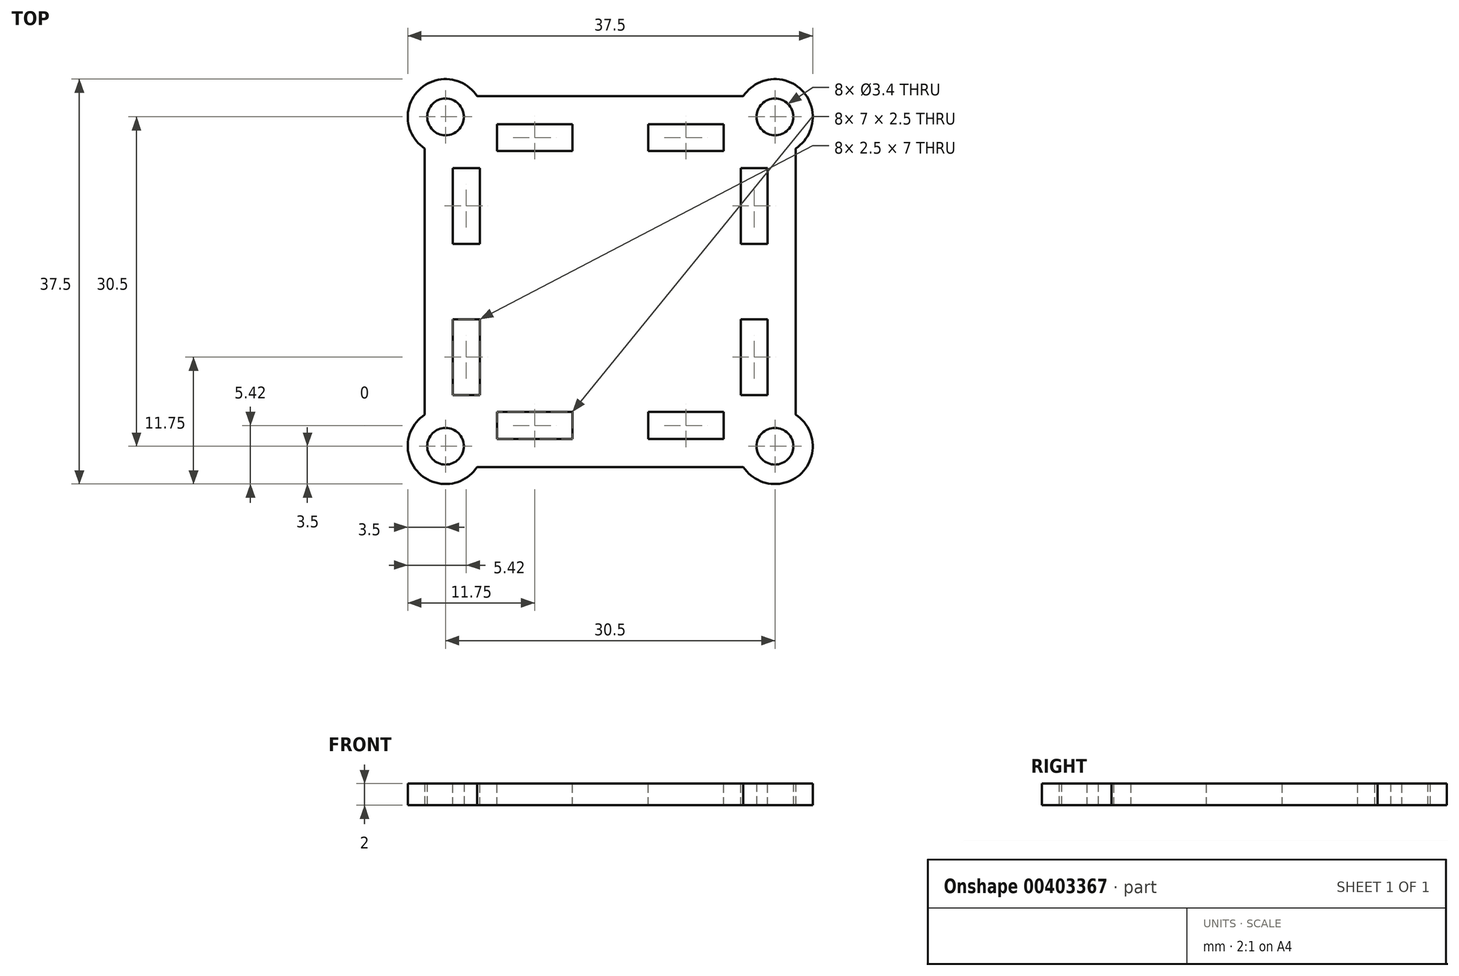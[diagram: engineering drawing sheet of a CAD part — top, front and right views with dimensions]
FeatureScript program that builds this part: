
annotation { "Feature Type Name" : "Feature", "Feature Type Description" : "" }
export const myFeature = defineFeature(function(context is Context, id is Id, definition is map)
    precondition{}
    {
        {
            assignVariable(context, id + "F0", {"name" : "padThickness", "anyValue" : 2});
        }
        {
            var Q0;
            Q0=qCreatedBy(makeId("Top.planeOp"),FACE);
            var sketch = newSketch(context, id + "F1", { "sketchPlane" : qUnion([Q0])});
            skLineSegment(sketch, "E0.bottom", {"start": v(15.25, -15.25) * mm, "end": v(-15.25, -15.25) * mm});
            skLineSegment(sketch, "E0.top", {"start": v(15.25, 15.25) * mm, "end": v(-15.25, 15.25) * mm});
            skLineSegment(sketch, "E0.left", {"start": v(15.25, -15.25) * mm, "end": v(15.25, 15.25) * mm});
            skLineSegment(sketch, "E0.right", {"start": v(-15.25, -15.25) * mm, "end": v(-15.25, 15.25) * mm});
            skPoint(sketch, "E0.middle", {"position": v(0, 0) * mm});
            skCircle(sketch, "E1", {"center": v(-15.25, 15.25) * mm, "radius": 1.7 * mm});
            skLineSegment(sketch, "E2", {"start": v(0, 15.25) * mm, "end": v(0, -15.25) * mm, "construction": true});
            skLineSegment(sketch, "E3", {"start": v(-15.25, 0) * mm, "end": v(15.25, 0) * mm, "construction": true});
            skCircle(sketch, "E4.MirrorC", {"center": v(15.25, 15.25) * mm, "radius": 1.7 * mm});
            skLineSegment(sketch, "E5.MirrorCS", {"start": v(15.25, 0) * mm, "end": v(-15.25, 0) * mm, "construction": true});
            skCircle(sketch, "E6.MirrorC", {"center": v(15.25, -15.25) * mm, "radius": 1.7 * mm});
            skCircle(sketch, "E7.MirrorC", {"center": v(-15.25, -15.25) * mm, "radius": 1.7 * mm});
            skCircle(sketch, "E8", {"center": v(-15.25, 15.25) * mm, "radius": 3.5 * mm});
            skCircle(sketch, "E9.MirrorC", {"center": v(15.25, 15.25) * mm, "radius": 3.5 * mm});
            skCircle(sketch, "E10.MirrorC", {"center": v(15.25, -15.25) * mm, "radius": 3.5 * mm});
            skCircle(sketch, "E11.MirrorC", {"center": v(-15.25, -15.25) * mm, "radius": 3.5 * mm});
            skLineSegment(sketch, "E12", {"start": v(-10.5, 15.25) * mm, "end": v(-10.5, -15.25) * mm, "construction": true});
            skLineSegment(sketch, "E13", {"start": v(10.5, 15.25) * mm, "end": v(10.5, -15.25) * mm, "construction": true});
            skLineSegment(sketch, "E14", {"start": v(-15.25, 17) * mm, "end": v(15.25, 17) * mm, "construction": true});
            skLineSegment(sketch, "E15", {"start": v(-15.25, -17) * mm, "end": v(15.25, -17) * mm, "construction": true});
            skLineSegment(sketch, "E16", {"start": v(-17.17, 12.32) * mm, "end": v(-17.17, -12.32) * mm});
            skLineSegment(sketch, "E17", {"start": v(-13.33, -12.32) * mm, "end": v(-13.33, 12.32) * mm});
            skLineSegment(sketch, "E18", {"start": v(-12.32, 17.17) * mm, "end": v(12.32, 17.17) * mm});
            skLineSegment(sketch, "E19", {"start": v(-12.32, 13.33) * mm, "end": v(12.32, 13.33) * mm});
            skLineSegment(sketch, "E20.MirrorCS", {"start": v(-12.32, -17.17) * mm, "end": v(12.32, -17.17) * mm});
            skLineSegment(sketch, "E21.MirrorCS", {"start": v(-12.32, -13.33) * mm, "end": v(12.32, -13.33) * mm});
            skLineSegment(sketch, "E22.MirrorCS", {"start": v(17.17, 12.32) * mm, "end": v(17.17, -12.32) * mm});
            skLineSegment(sketch, "E23.MirrorCS", {"start": v(13.33, -12.32) * mm, "end": v(13.33, 12.32) * mm});
            skPoint(sketch, "E24", {"position": v(0, 17) * mm});
            skPoint(sketch, "E25", {"position": v(0, 18.92) * mm});
            skSolve(sketch);
        }
        {
            var Q0;
            {var subQ1=sQuery(id+"F1.wireOp",EDGE,"E0.top");var subQ5=sQuery(id+"F1.wireOp",EDGE,"E8");var subQ7=makeQuery(id+"F1.imprint","INTERSECT",VERTEX,{"derivedFrom":[subQ1,subQ5]});Q0=makeQuery(id+"F1.imprint","IMPRINT",FACE,{"disambiguationData":[TD([[makeQuery(id+"F1.imprint","IMPRINT",EDGE,{"disambiguationData":[TD([[subQ7,-1.0]])],"derivedFrom":subQ1}),-1.0]])]});}
            var Q1;
            {var subQ0=sQuery(id+"F1.wireOp",EDGE,"E8");var subQ5=sQuery(id+"F1.wireOp",EDGE,"E0.top");var subQ9=makeQuery(id+"F1.imprint","INTERSECT",VERTEX,{"derivedFrom":[subQ5,subQ0]});Q1=makeQuery(id+"F1.imprint","IMPRINT",FACE,{"disambiguationData":[TD([[makeQuery(id+"F1.imprint","IMPRINT",EDGE,{"disambiguationData":[TD([[subQ9,-1.0]])],"derivedFrom":subQ5}),1.0]])]});}
            var Q2;
            {var subQ2=sQuery(id+"F1.wireOp",EDGE,"E0.top");var subQ4=sQuery(id+"F1.wireOp",EDGE,"E4.MirrorC");var subQ5=makeQuery(id+"F1.imprint","INTERSECT",VERTEX,{"derivedFrom":[subQ2,subQ4]});Q2=makeQuery(id+"F1.imprint","IMPRINT",FACE,{"disambiguationData":[TD([[makeQuery(id+"F1.imprint","IMPRINT",EDGE,{"disambiguationData":[TD([[subQ5,-1.0]])],"derivedFrom":subQ2}),-1.0]])]});}
            var Q3;
            {var subQ4=sQuery(id+"F1.wireOp",EDGE,"E4.MirrorC");var subQ5=sQuery(id+"F1.wireOp",EDGE,"E0.top");var subQ6=makeQuery(id+"F1.imprint","INTERSECT",VERTEX,{"derivedFrom":[subQ5,subQ4]});Q3=makeQuery(id+"F1.imprint","IMPRINT",FACE,{"disambiguationData":[TD([[makeQuery(id+"F1.imprint","IMPRINT",EDGE,{"disambiguationData":[TD([[subQ6,-1.0]])],"derivedFrom":subQ5}),1.0]])]});}
            var Q4;
            {var subQ5=sQuery(id+"F1.wireOp",EDGE,"E23.MirrorCS");Q4=makeQuery(id+"F1.imprint","IMPRINT",FACE,{"disambiguationData":[TD([[makeQuery(id+"F1.imprint","IMPRINT",EDGE,{"derivedFrom":subQ5}),-1.0]])]});}
            var Q5;
            {var subQ5=sQuery(id+"F1.wireOp",EDGE,"E19");Q5=makeQuery(id+"F1.imprint","IMPRINT",FACE,{"disambiguationData":[TD([[makeQuery(id+"F1.imprint","IMPRINT",EDGE,{"derivedFrom":subQ5}),1.0]])]});}
            var Q6;
            {var subQ5=sQuery(id+"F1.wireOp",EDGE,"E17");Q6=makeQuery(id+"F1.imprint","IMPRINT",FACE,{"disambiguationData":[TD([[makeQuery(id+"F1.imprint","IMPRINT",EDGE,{"derivedFrom":subQ5}),1.0]])]});}
            var Q7;
            {var subQ5=sQuery(id+"F1.wireOp",EDGE,"E16");Q7=makeQuery(id+"F1.imprint","IMPRINT",FACE,{"disambiguationData":[TD([[makeQuery(id+"F1.imprint","IMPRINT",EDGE,{"derivedFrom":subQ5}),1.0]])]});}
            var Q8;
            {var subQ5=sQuery(id+"F1.wireOp",EDGE,"E22.MirrorCS");Q8=makeQuery(id+"F1.imprint","IMPRINT",FACE,{"disambiguationData":[TD([[makeQuery(id+"F1.imprint","IMPRINT",EDGE,{"derivedFrom":subQ5}),-1.0]])]});}
            var Q9;
            {var subQ5=sQuery(id+"F1.wireOp",EDGE,"E21.MirrorCS");Q9=makeQuery(id+"F1.imprint","IMPRINT",FACE,{"disambiguationData":[TD([[makeQuery(id+"F1.imprint","IMPRINT",EDGE,{"derivedFrom":subQ5}),-1.0]])]});}
            var Q10;
            {var subQ5=sQuery(id+"F1.wireOp",EDGE,"E20.MirrorCS");Q10=makeQuery(id+"F1.imprint","IMPRINT",FACE,{"disambiguationData":[TD([[makeQuery(id+"F1.imprint","IMPRINT",EDGE,{"derivedFrom":subQ5}),1.0]])]});}
            var Q11;
            {var subQ5=sQuery(id+"F1.wireOp",EDGE,"E18");Q11=makeQuery(id+"F1.imprint","IMPRINT",FACE,{"disambiguationData":[TD([[makeQuery(id+"F1.imprint","IMPRINT",EDGE,{"derivedFrom":subQ5}),-1.0]])]});}
            var Q12;
            {var subQ0=sQuery(id+"F1.wireOp",EDGE,"E11.MirrorC");var subQ2=sQuery(id+"F1.wireOp",EDGE,"E0.bottom");var subQ3=makeQuery(id+"F1.imprint","INTERSECT",VERTEX,{"derivedFrom":[subQ2,subQ0]});Q12=makeQuery(id+"F1.imprint","IMPRINT",FACE,{"disambiguationData":[TD([[makeQuery(id+"F1.imprint","IMPRINT",EDGE,{"disambiguationData":[TD([[subQ3,-1.0]])],"derivedFrom":subQ2}),1.0]])]});}
            var Q13;
            {var subQ0=sQuery(id+"F1.wireOp",EDGE,"E11.MirrorC");var subQ5=sQuery(id+"F1.wireOp",EDGE,"E0.bottom");var subQ8=makeQuery(id+"F1.imprint","INTERSECT",VERTEX,{"derivedFrom":[subQ5,subQ0]});Q13=makeQuery(id+"F1.imprint","IMPRINT",FACE,{"disambiguationData":[TD([[makeQuery(id+"F1.imprint","IMPRINT",EDGE,{"disambiguationData":[TD([[subQ8,-1.0]])],"derivedFrom":subQ5}),-1.0]])]});}
            var Q14;
            {var subQ4=sQuery(id+"F1.wireOp",EDGE,"E6.MirrorC");var subQ5=sQuery(id+"F1.wireOp",EDGE,"E0.bottom");var subQ6=makeQuery(id+"F1.imprint","INTERSECT",VERTEX,{"derivedFrom":[subQ5,subQ4]});Q14=makeQuery(id+"F1.imprint","IMPRINT",FACE,{"disambiguationData":[TD([[makeQuery(id+"F1.imprint","IMPRINT",EDGE,{"disambiguationData":[TD([[subQ6,-1.0]])],"derivedFrom":subQ5}),-1.0]])]});}
            var Q15;
            {var subQ2=sQuery(id+"F1.wireOp",EDGE,"E0.bottom");var subQ4=sQuery(id+"F1.wireOp",EDGE,"E6.MirrorC");var subQ5=makeQuery(id+"F1.imprint","INTERSECT",VERTEX,{"derivedFrom":[subQ2,subQ4]});Q15=makeQuery(id+"F1.imprint","IMPRINT",FACE,{"disambiguationData":[TD([[makeQuery(id+"F1.imprint","IMPRINT",EDGE,{"disambiguationData":[TD([[subQ5,-1.0]])],"derivedFrom":subQ2}),1.0]])]});}
            var Q16;
            {var subQ0=sQuery(id+"F1.wireOp",EDGE,"E17");Q16=makeQuery(id+"F1.imprint","IMPRINT",FACE,{"disambiguationData":[TD([[makeQuery(id+"F1.imprint","IMPRINT",EDGE,{"derivedFrom":subQ0}),-1.0]])]});}
            extrude(context, id + "F2", {"entities" : qUnion([Q0, Q1, Q2, Q3, Q4, Q5, Q6, Q7, Q8, Q9, Q10, Q11, Q12, Q13, Q14, Q15, Q16]), "depth" : (getVariable(context, 'padThickness')) * mm});
        }
        {
            var Q0;
            Q0=qCreatedBy(makeId("Front.planeOp"),FACE);
            var sketch = newSketch(context, id + "F3", { "sketchPlane" : qUnion([Q0])});
            skLineSegment(sketch, "E26", {"start": v(0, 0) * mm, "end": v(0, 87.17) * mm, "construction": true});
            skSolve(sketch);
        }
        {
            var Q0;
            Q0=makeQuery(id+"F2.opExtrude","SWEPT_BODY",BODY,{"disambiguationData":[OSD([sQuery(id+"F1.wireOp",EDGE,"E1"),sQuery(id+"F1.wireOp",EDGE,"E4.MirrorC"),sQuery(id+"F1.wireOp",EDGE,"E6.MirrorC"),sQuery(id+"F1.wireOp",EDGE,"E7.MirrorC"),sQuery(id+"F1.wireOp",EDGE,"E8"),sQuery(id+"F1.wireOp",EDGE,"E9.MirrorC"),sQuery(id+"F1.wireOp",EDGE,"E10.MirrorC"),sQuery(id+"F1.wireOp",EDGE,"E11.MirrorC"),sQuery(id+"F1.wireOp",EDGE,"E16"),sQuery(id+"F1.wireOp",EDGE,"E18"),sQuery(id+"F1.wireOp",EDGE,"E20.MirrorCS"),sQuery(id+"F1.wireOp",EDGE,"E22.MirrorCS")])]});
            var Q1;
            Q1=sQuery(id+"F3.wireOp",EDGE,"E26");
            transform(context, id + "F4", {"entities" : qUnion([Q0]), "transformType" : TransformType.ROTATION, "transformAxis" : qUnion([Q1]), "angle" : 45 * degree, "makeCopy" : true});
        }
        {
            var Q0;
            Q0=makeQuery(id+"F2.opExtrude","SWEPT_BODY",BODY,{"disambiguationData":[OSD([sQuery(id+"F1.wireOp",EDGE,"E1"),sQuery(id+"F1.wireOp",EDGE,"E4.MirrorC"),sQuery(id+"F1.wireOp",EDGE,"E6.MirrorC"),sQuery(id+"F1.wireOp",EDGE,"E7.MirrorC"),sQuery(id+"F1.wireOp",EDGE,"E8"),sQuery(id+"F1.wireOp",EDGE,"E9.MirrorC"),sQuery(id+"F1.wireOp",EDGE,"E10.MirrorC"),sQuery(id+"F1.wireOp",EDGE,"E11.MirrorC"),sQuery(id+"F1.wireOp",EDGE,"E16"),sQuery(id+"F1.wireOp",EDGE,"E18"),sQuery(id+"F1.wireOp",EDGE,"E20.MirrorCS"),sQuery(id+"F1.wireOp",EDGE,"E22.MirrorCS")])]});
            var Q1;
            Q1=makeQuery(id+"F4.opPattern","COPY",BODY,{"derivedFrom":makeQuery(id+"F2.opExtrude","SWEPT_BODY",BODY,{"disambiguationData":[OSD([sQuery(id+"F1.wireOp",EDGE,"E1"),sQuery(id+"F1.wireOp",EDGE,"E4.MirrorC"),sQuery(id+"F1.wireOp",EDGE,"E6.MirrorC"),sQuery(id+"F1.wireOp",EDGE,"E7.MirrorC"),sQuery(id+"F1.wireOp",EDGE,"E8"),sQuery(id+"F1.wireOp",EDGE,"E9.MirrorC"),sQuery(id+"F1.wireOp",EDGE,"E10.MirrorC"),sQuery(id+"F1.wireOp",EDGE,"E11.MirrorC"),sQuery(id+"F1.wireOp",EDGE,"E16"),sQuery(id+"F1.wireOp",EDGE,"E18"),sQuery(id+"F1.wireOp",EDGE,"E20.MirrorCS"),sQuery(id+"F1.wireOp",EDGE,"E22.MirrorCS")])]}),"instanceName":"1"});
            booleanBodies(context, id + "F5", {"operationType" : BooleanOperationType.UNION, "tools" : qUnion([Q0, Q1])});
        }
        {
            var Q0;
            Q0=makeQuery(id+"F2.opExtrude","CAP_FACE",FACE,{"disambiguationData":[OSD([sQuery(id+"F1.wireOp",EDGE,"E1"),sQuery(id+"F1.wireOp",EDGE,"E4.MirrorC"),sQuery(id+"F1.wireOp",EDGE,"E6.MirrorC"),sQuery(id+"F1.wireOp",EDGE,"E7.MirrorC"),sQuery(id+"F1.wireOp",EDGE,"E8"),sQuery(id+"F1.wireOp",EDGE,"E9.MirrorC"),sQuery(id+"F1.wireOp",EDGE,"E10.MirrorC"),sQuery(id+"F1.wireOp",EDGE,"E11.MirrorC"),sQuery(id+"F1.wireOp",EDGE,"E16"),sQuery(id+"F1.wireOp",EDGE,"E18"),sQuery(id+"F1.wireOp",EDGE,"E20.MirrorCS"),sQuery(id+"F1.wireOp",EDGE,"E22.MirrorCS")])],"isStart":false});
            var sketch = newSketch(context, id + "F6", { "sketchPlane" : qUnion([Q0])});
            skLineSegment(sketch, "E27.0", {"start": v(-10.5, 15.25) * mm, "end": v(-10.5, -15.25) * mm, "construction": true});
            skLineSegment(sketch, "E27.1", {"start": v(-12.32, 13.33) * mm, "end": v(12.32, 13.33) * mm, "construction": true});
            skLineSegment(sketch, "E27.2", {"start": v(10.5, 15.25) * mm, "end": v(10.5, -15.25) * mm, "construction": true});
            skLineSegment(sketch, "E27.3", {"start": v(-12.32, -13.33) * mm, "end": v(12.32, -13.33) * mm, "construction": true});
            skText(sketch, "E28", { "text": "tits", "fontName": "AllertaStencil-Regular.ttf"});
            skPoint(sketch, "E29", {"position": v(0, 0) * mm});
            const initialGuessF6  = {"E28": [-0.015, -0.00666, 1, 0, 0.01332]};
            skSetInitialGuess(sketch, initialGuessF6);
            skSolve(sketch);
        }
        {
            var Q0;
            {var subQ0=makeQuery(id+"F2.opExtrude","CAP_FACE",FACE,{"disambiguationData":[OSD([sQuery(id+"F1.wireOp",EDGE,"E1"),sQuery(id+"F1.wireOp",EDGE,"E4.MirrorC"),sQuery(id+"F1.wireOp",EDGE,"E6.MirrorC"),sQuery(id+"F1.wireOp",EDGE,"E7.MirrorC"),sQuery(id+"F1.wireOp",EDGE,"E8"),sQuery(id+"F1.wireOp",EDGE,"E9.MirrorC"),sQuery(id+"F1.wireOp",EDGE,"E10.MirrorC"),sQuery(id+"F1.wireOp",EDGE,"E11.MirrorC"),sQuery(id+"F1.wireOp",EDGE,"E16"),sQuery(id+"F1.wireOp",EDGE,"E18"),sQuery(id+"F1.wireOp",EDGE,"E20.MirrorCS"),sQuery(id+"F1.wireOp",EDGE,"E22.MirrorCS")])],"isStart":false});Q0=makeQuery(id+"F5.opBoolean","MERGE",FACE,{"derivedFrom":[subQ0,makeQuery(id+"F4.opPattern","COPY",FACE,{"derivedFrom":subQ0,"instanceName":"1"})]});}
            var sketch = newSketch(context, id + "F7", { "sketchPlane" : qUnion([Q0])});
            skLineSegment(sketch, "E30.0", {"start": v(15.25, -15.25) * mm, "end": v(15.25, 15.25) * mm, "construction": true});
            skLineSegment(sketch, "E30.1", {"start": v(15.25, 15.25) * mm, "end": v(-15.25, 15.25) * mm, "construction": true});
            skLineSegment(sketch, "E30.2", {"start": v(-15.25, -15.25) * mm, "end": v(-15.25, 15.25) * mm, "construction": true});
            skLineSegment(sketch, "E30.3", {"start": v(15.25, -15.25) * mm, "end": v(-15.25, -15.25) * mm, "construction": true});
            skLineSegment(sketch, "E31", {"start": v(-15.25, 15.25) * mm, "end": v(15.25, -15.25) * mm, "construction": true});
            skLineSegment(sketch, "E32", {"start": v(21.57, 0) * mm, "end": v(-21.57, 0) * mm, "construction": true});
            skLineSegment(sketch, "E33", {"start": v(0, 21.57) * mm, "end": v(0, -21.57) * mm, "construction": true});
            skLineSegment(sketch, "E34", {"start": v(-15.25, -15.25) * mm, "end": v(15.25, 15.25) * mm, "construction": true});
            skCircle(sketch, "E35.0", {"center": v(-15.25, 15.25) * mm, "radius": 3.5 * mm, "construction": true});
            skLineSegment(sketch, "E36.0", {"start": v(-13.33, -12.32) * mm, "end": v(-13.33, -5.63) * mm, "construction": true});
            skLineSegment(sketch, "E37.0", {"start": v(-10.61, 13.33) * mm, "end": v(10.61, 13.33) * mm});
            skLineSegment(sketch, "E37.1", {"start": v(13.33, -12.32) * mm, "end": v(13.33, -5.63) * mm, "construction": true});
            skLineSegment(sketch, "E38.0", {"start": v(-10.61, -13.33) * mm, "end": v(10.61, -13.33) * mm});
            skCircle(sketch, "E39.0", {"center": v(15.25, -15.25) * mm, "radius": 3.5 * mm, "construction": true});
            skCircle(sketch, "E40.0", {"center": v(-15.25, -15.25) * mm, "radius": 3.5 * mm, "construction": true});
            skLineSegment(sketch, "E41.0", {"start": v(-12.32, 17.17) * mm, "end": v(12.32, 17.17) * mm});
            skLineSegment(sketch, "E42.0", {"start": v(-15.25, -17) * mm, "end": v(15.25, -17) * mm, "construction": true});
            skLineSegment(sketch, "E43.0", {"start": v(-17.17, 12.32) * mm, "end": v(-17.17, -12.32) * mm, "construction": true});
            skLineSegment(sketch, "E44.0", {"start": v(17.17, 12.32) * mm, "end": v(17.17, -12.32) * mm, "construction": true});
            skPoint(sketch, "E45", {"position": v(-12.32, 13.33) * mm});
            skPoint(sketch, "E46", {"position": v(-13.33, 12.32) * mm});
            skCircle(sketch, "E47.0", {"center": v(15.25, 15.25) * mm, "radius": 3.5 * mm, "construction": true});
            skLineSegment(sketch, "E48", {"start": v(-17.17, 7.11) * mm, "end": v(-1.92, 7.11) * mm, "construction": true});
            skLineSegment(sketch, "E49", {"start": v(-17.17, -7.11) * mm, "end": v(-1.92, -7.11) * mm, "construction": true});
            skPoint(sketch, "E50", {"position": v(0, 7.11) * mm});
            skPoint(sketch, "E51", {"position": v(0, -7.11) * mm});
            skArc(sketch, "E52", {"start": v(13.33, 5.63) * mm, "mid": v(11.24, 6.06) * mm, "end": v(9.14, 6.42) * mm});
            skPoint(sketch, "E53", {"position": v(-13.33, 5.63) * mm});
            skPoint(sketch, "E54", {"position": v(13.33, 5.63) * mm});
            skPoint(sketch, "E55.MirrorP", {"position": v(13.33, -5.63) * mm});
            skPoint(sketch, "E56.MirrorP", {"position": v(-13.33, -5.63) * mm});
            skArc(sketch, "E57.MirrorCS", {"start": v(13.33, -5.63) * mm, "mid": v(11.24, -6.06) * mm, "end": v(9.14, -6.42) * mm});
            skPoint(sketch, "E58.trimOffspring.end.orphan", {"position": v(-20.86, 3.43) * mm});
            skPoint(sketch, "E59.orphan", {"position": v(20.86, 3.43) * mm});
            skPoint(sketch, "E60.orphan", {"position": v(20.86, -3.43) * mm});
            skPoint(sketch, "E61.orphan", {"position": v(-20.86, -3.43) * mm});
            skLineSegment(sketch, "E62.0", {"start": v(-1.92, 13.33) * mm, "end": v(-1.92, 7.08) * mm});
            skPoint(sketch, "E63.orphan", {"position": v(-1.92, 21.57) * mm});
            skPoint(sketch, "E64.orphan", {"position": v(1.92, 21.57) * mm});
            skPoint(sketch, "E65.orphan", {"position": v(1.92, -21.57) * mm});
            skPoint(sketch, "E66.orphan", {"position": v(-1.92, -21.57) * mm});
            skLineSegment(sketch, "E67.0", {"start": v(-10.61, 13.33) * mm, "end": v(16.6, -13.9) * mm, "construction": true});
            skLineSegment(sketch, "E68.MirrorCS", {"start": v(-13.33, 10.61) * mm, "end": v(13.9, -16.6) * mm, "construction": true});
            skPoint(sketch, "E69.orphan", {"position": v(-13.9, 16.6) * mm});
            skPoint(sketch, "E70.orphan", {"position": v(-16.6, 13.9) * mm});
            skLineSegment(sketch, "E71.0", {"start": v(-16.6, -13.9) * mm, "end": v(-15.25, -12.53) * mm, "construction": true});
            skLineSegment(sketch, "E72.MirrorCS", {"start": v(-13.9, -16.6) * mm, "end": v(16.6, 13.9) * mm, "construction": true});
            skPoint(sketch, "E73.orphan", {"position": v(12.32, 13.33) * mm});
            skPoint(sketch, "E74.orphan", {"position": v(13.33, 12.32) * mm});
            skPoint(sketch, "E75.orphan", {"position": v(-12.32, -13.33) * mm});
            skPoint(sketch, "E76.orphan", {"position": v(12.32, -13.33) * mm});
            skLineSegment(sketch, "E77.trimOffspring", {"start": v(-13.33, 5.63) * mm, "end": v(-13.33, 10.61) * mm, "construction": true});
            skLineSegment(sketch, "E78.trimOffspring", {"start": v(13.33, 5.63) * mm, "end": v(13.33, 10.61) * mm, "construction": true});
            skLineSegment(sketch, "E79", {"start": v(-13.33, 10.61) * mm, "end": v(-13.33, 5.63) * mm});
            skLineSegment(sketch, "E80", {"start": v(-13.33, -5.63) * mm, "end": v(-13.33, -10.61) * mm});
            skLineSegment(sketch, "E81.trimOffspring", {"start": v(-14.54, -11.82) * mm, "end": v(13.9, 16.6) * mm, "construction": true});
            skLineSegment(sketch, "E82", {"start": v(-10.61, 13.33) * mm, "end": v(-4.25, 6.96) * mm});
            skLineSegment(sketch, "E83", {"start": v(-9.14, 6.42) * mm, "end": v(-13.33, 10.61) * mm});
            skLineSegment(sketch, "E84", {"start": v(10.61, 13.33) * mm, "end": v(4.25, 6.96) * mm});
            skLineSegment(sketch, "E85", {"start": v(13.33, 10.61) * mm, "end": v(9.14, 6.42) * mm});
            skLineSegment(sketch, "E86", {"start": v(-9.14, -6.42) * mm, "end": v(-13.33, -10.61) * mm});
            skLineSegment(sketch, "E87", {"start": v(-10.61, -13.33) * mm, "end": v(-4.25, -6.96) * mm});
            skLineSegment(sketch, "E88", {"start": v(4.25, -6.96) * mm, "end": v(10.61, -13.33) * mm});
            skLineSegment(sketch, "E89", {"start": v(9.14, -6.42) * mm, "end": v(13.33, -10.61) * mm});
            skLineSegment(sketch, "E90", {"start": v(13.33, -10.61) * mm, "end": v(13.33, -5.63) * mm});
            skLineSegment(sketch, "E91", {"start": v(13.33, 10.61) * mm, "end": v(13.33, 5.63) * mm});
            skLineSegment(sketch, "E92.MirrorCS", {"start": v(1.92, 13.33) * mm, "end": v(1.92, 7.08) * mm});
            skLineSegment(sketch, "E93.MirrorCS", {"start": v(-1.92, -13.33) * mm, "end": v(-1.92, -7.08) * mm});
            skLineSegment(sketch, "E94.MirrorCS", {"start": v(1.92, -13.33) * mm, "end": v(1.92, -7.08) * mm});
            skArc(sketch, "E95.trimOffspring", {"start": v(-9.14, 6.42) * mm, "mid": v(-11.24, 6.06) * mm, "end": v(-13.33, 5.63) * mm});
            skArc(sketch, "E96.trimOffspring", {"start": v(-1.92, 7.08) * mm, "mid": v(-3.08, 7.03) * mm, "end": v(-4.25, 6.96) * mm});
            skLineSegment(sketch, "E97.trimOffspring", {"start": v(0, 7.11) * mm, "end": v(17.17, 7.11) * mm, "construction": true});
            skArc(sketch, "E98.trimOffspring", {"start": v(4.25, 6.96) * mm, "mid": v(3.08, 7.03) * mm, "end": v(1.92, 7.08) * mm});
            skArc(sketch, "E99.trimOffspring", {"start": v(-9.14, -6.42) * mm, "mid": v(-11.24, -6.06) * mm, "end": v(-13.33, -5.63) * mm});
            skLineSegment(sketch, "E100.trimOffspring", {"start": v(1.92, -7.11) * mm, "end": v(17.17, -7.11) * mm, "construction": true});
            skArc(sketch, "E101.trimOffspring", {"start": v(4.25, -6.96) * mm, "mid": v(3.08, -7.03) * mm, "end": v(1.92, -7.08) * mm});
            skArc(sketch, "E102.trimOffspring", {"start": v(-1.92, -7.08) * mm, "mid": v(-3.08, -7.03) * mm, "end": v(-4.25, -6.96) * mm});
            skSolve(sketch);
        }
        {
            var Q0;
            {var subQ0=makeQuery(id+"F2.opExtrude","CAP_FACE",FACE,{"disambiguationData":[OSD([sQuery(id+"F1.wireOp",EDGE,"E1"),sQuery(id+"F1.wireOp",EDGE,"E4.MirrorC"),sQuery(id+"F1.wireOp",EDGE,"E6.MirrorC"),sQuery(id+"F1.wireOp",EDGE,"E7.MirrorC"),sQuery(id+"F1.wireOp",EDGE,"E8"),sQuery(id+"F1.wireOp",EDGE,"E9.MirrorC"),sQuery(id+"F1.wireOp",EDGE,"E10.MirrorC"),sQuery(id+"F1.wireOp",EDGE,"E11.MirrorC"),sQuery(id+"F1.wireOp",EDGE,"E16"),sQuery(id+"F1.wireOp",EDGE,"E18"),sQuery(id+"F1.wireOp",EDGE,"E20.MirrorCS"),sQuery(id+"F1.wireOp",EDGE,"E22.MirrorCS")])],"isStart":false});Q0=makeQuery(id+"F5.opBoolean","MERGE",FACE,{"derivedFrom":[subQ0,makeQuery(id+"F4.opPattern","COPY",FACE,{"derivedFrom":subQ0,"instanceName":"1"})]});}
            var sketch = newSketch(context, id + "F8", { "sketchPlane" : qUnion([Q0])});
            skLineSegment(sketch, "E103", {"start": v(-17.17, 7.11) * mm, "end": v(-17.17, -7.11) * mm});
            skLineSegment(sketch, "E104", {"start": v(-7.11, -17.17) * mm, "end": v(7.11, -17.17) * mm});
            skLineSegment(sketch, "E105", {"start": v(17.17, -7.11) * mm, "end": v(17.17, 7.11) * mm});
            skLineSegment(sketch, "E106", {"start": v(7.11, 17.17) * mm, "end": v(-7.11, 17.17) * mm});
            skSolve(sketch);
        }
        {
            var Q0;
            Q0=makeQuery(id+"F8.imprint","IMPRINT",FACE,{"disambiguationData":[TD([[makeQuery(id+"F8.imprint","IMPRINT",EDGE,{"derivedFrom":sQuery(id+"F8.wireOp",EDGE,"E106")}),-1.0]])]});
            var Q1;
            Q1=makeQuery(id+"F8.imprint","IMPRINT",FACE,{"disambiguationData":[TD([[makeQuery(id+"F8.imprint","IMPRINT",EDGE,{"derivedFrom":sQuery(id+"F8.wireOp",EDGE,"E105")}),-1.0]])]});
            var Q2;
            Q2=makeQuery(id+"F8.imprint","IMPRINT",FACE,{"disambiguationData":[TD([[makeQuery(id+"F8.imprint","IMPRINT",EDGE,{"derivedFrom":sQuery(id+"F8.wireOp",EDGE,"E104")}),-1.0]])]});
            var Q3;
            Q3=makeQuery(id+"F8.imprint","IMPRINT",FACE,{"disambiguationData":[TD([[makeQuery(id+"F8.imprint","IMPRINT",EDGE,{"derivedFrom":sQuery(id+"F8.wireOp",EDGE,"E103")}),-1.0]])]});
            extrude(context, id + "F9", {"entities" : qUnion([Q0, Q1, Q2, Q3]), "operationType" : NewBodyOperationType.REMOVE, "endBound" : BoundingType.THROUGH_ALL, "oppositeDirection" : true, "depth" : 25 * mm});
        }
        {
            var Q0;
            Q0=makeQuery(id+"F7.imprint","IMPRINT",FACE,{"disambiguationData":[TD([[makeQuery(id+"F7.imprint","IMPRINT",EDGE,{"derivedFrom":sQuery(id+"F7.wireOp",EDGE,"E52")}),1.0]])]});
            var sketch = newSketch(context, id + "F10", { "sketchPlane" : qUnion([Q0])});
            skLineSegment(sketch, "E107.0", {"start": v(0, 21.57) * mm, "end": v(0, -21.57) * mm, "construction": true});
            skLineSegment(sketch, "E108.0", {"start": v(21.57, 0) * mm, "end": v(-21.57, 0) * mm, "construction": true});
            skLineSegment(sketch, "E109.0", {"start": v(-12.32, 17.17) * mm, "end": v(12.32, 17.17) * mm});
            skLineSegment(sketch, "E110.0", {"start": v(-17.17, 12.32) * mm, "end": v(-17.17, -12.32) * mm, "construction": true});
            skLineSegment(sketch, "E111.0", {"start": v(17.17, 12.32) * mm, "end": v(17.17, -12.32) * mm, "construction": true});
            skLineSegment(sketch, "E112.0", {"start": v(-10.61, 13.33) * mm, "end": v(10.61, 13.33) * mm, "construction": true});
            skPoint(sketch, "E113", {"position": v(0, 13.33) * mm});
            skPoint(sketch, "E114", {"position": v(57.37, 5.4) * mm});
            skLineSegment(sketch, "E115", {"start": v(-7, 17.17) * mm, "end": v(-7, -17.67) * mm, "construction": true});
            skLineSegment(sketch, "E116", {"start": v(7, 17.17) * mm, "end": v(7, -17.67) * mm, "construction": true});
            skPoint(sketch, "E117", {"position": v(-7, 13.33) * mm});
            skPoint(sketch, "E118", {"position": v(7, 13.33) * mm});
            skLineSegment(sketch, "E119.bottom", {"start": v(-3.5, 12.08) * mm, "end": v(-10.5, 12.08) * mm});
            skLineSegment(sketch, "E119.top", {"start": v(-3.5, 14.58) * mm, "end": v(-10.5, 14.58) * mm});
            skLineSegment(sketch, "E119.left", {"start": v(-3.5, 12.08) * mm, "end": v(-3.5, 14.58) * mm});
            skLineSegment(sketch, "E119.right", {"start": v(-10.5, 12.08) * mm, "end": v(-10.5, 14.58) * mm});
            skLineSegment(sketch, "E120.MirrorCS", {"start": v(10.5, 12.08) * mm, "end": v(10.5, 14.58) * mm});
            skLineSegment(sketch, "E121.MirrorCS", {"start": v(3.5, 12.08) * mm, "end": v(3.5, 14.58) * mm});
            skLineSegment(sketch, "E122.MirrorCS", {"start": v(3.5, 14.58) * mm, "end": v(10.5, 14.58) * mm});
            skLineSegment(sketch, "E123.MirrorCS", {"start": v(3.5, 12.08) * mm, "end": v(10.5, 12.08) * mm});
            skLineSegment(sketch, "E124.MirrorCS", {"start": v(10.5, 14.58) * mm, "end": v(10.5, 12.08) * mm});
            skLineSegment(sketch, "E125.MirrorCS", {"start": v(-10.5, 14.58) * mm, "end": v(-10.5, 12.08) * mm});
            skLineSegment(sketch, "E126.MirrorCS", {"start": v(-3.5, 14.58) * mm, "end": v(-3.5, 12.08) * mm});
            skLineSegment(sketch, "E127.MirrorCS", {"start": v(3.5, 14.58) * mm, "end": v(3.5, 12.08) * mm});
            skLineSegment(sketch, "E128.MirrorCS", {"start": v(21.57, 26.66) * mm, "end": v(-21.57, 26.66) * mm, "construction": true});
            skLineSegment(sketch, "E129.MirrorCS", {"start": v(10.5, -12.08) * mm, "end": v(10.5, -14.58) * mm});
            skLineSegment(sketch, "E130.MirrorCS", {"start": v(3.5, -14.58) * mm, "end": v(10.5, -14.58) * mm});
            skLineSegment(sketch, "E131.MirrorCS", {"start": v(3.5, -12.08) * mm, "end": v(10.5, -12.08) * mm});
            skLineSegment(sketch, "E132.MirrorCS", {"start": v(3.5, -12.08) * mm, "end": v(3.5, -14.58) * mm});
            skLineSegment(sketch, "E133.MirrorCS", {"start": v(-3.5, -12.08) * mm, "end": v(-3.5, -14.58) * mm});
            skLineSegment(sketch, "E134.MirrorCS", {"start": v(-3.5, -12.08) * mm, "end": v(-10.5, -12.08) * mm});
            skLineSegment(sketch, "E135.MirrorCS", {"start": v(-3.5, -14.58) * mm, "end": v(-10.5, -14.58) * mm});
            skLineSegment(sketch, "E136.MirrorCS", {"start": v(-10.5, -12.08) * mm, "end": v(-10.5, -14.58) * mm});
            skLineSegment(sketch, "E137.MirrorCS", {"start": v(-10.61, -13.33) * mm, "end": v(10.61, -13.33) * mm, "construction": true});
            skSolve(sketch);
        }
        {
            var Q0;
            {var subQ5=sQuery(id+"F10.wireOp",EDGE,"E119.top");Q0=makeQuery(id+"F10.imprint","IMPRINT",FACE,{"disambiguationData":[TD([[makeQuery(id+"F10.imprint","IMPRINT",EDGE,{"derivedFrom":subQ5}),1.0]])]});}
            var Q1;
            {var subQ0=sQuery(id+"F10.wireOp",EDGE,"E119.bottom");var subQ1=sQuery(id+"F10.wireOp",EDGE,"E119.left");var subQ2=makeQuery(id+"F10.imprint","INTERSECT",VERTEX,{"derivedFrom":[subQ1,subQ0]});Q1=makeQuery(id+"F10.imprint","IMPRINT",FACE,{"disambiguationData":[TD([[makeQuery(id+"F10.imprint","IMPRINT",EDGE,{"disambiguationData":[TD([[subQ2,-1.0]])],"derivedFrom":subQ0}),-1.0]])]});}
            var Q2;
            {var subQ0=sQuery(id+"F10.wireOp",EDGE,"E127.MirrorCS");var subQ1=sQuery(id+"F10.wireOp",EDGE,"E123.MirrorCS");var subQ2=makeQuery(id+"F10.imprint","INTERSECT",VERTEX,{"derivedFrom":[subQ1,subQ0]});Q2=makeQuery(id+"F10.imprint","IMPRINT",FACE,{"disambiguationData":[TD([[makeQuery(id+"F10.imprint","IMPRINT",EDGE,{"disambiguationData":[TD([[subQ2,-1.0]])],"derivedFrom":subQ1}),1.0]])]});}
            var Q3;
            {var subQ1=sQuery(id+"F10.wireOp",EDGE,"E122.MirrorCS");Q3=makeQuery(id+"F10.imprint","IMPRINT",FACE,{"disambiguationData":[TD([[makeQuery(id+"F10.imprint","IMPRINT",EDGE,{"derivedFrom":subQ1}),-1.0]])]});}
            var Q4;
            {var subQ0=sQuery(id+"F10.wireOp",EDGE,"E132.MirrorCS");var subQ1=sQuery(id+"F10.wireOp",EDGE,"E131.MirrorCS");var subQ2=makeQuery(id+"F10.imprint","INTERSECT",VERTEX,{"derivedFrom":[subQ1,subQ0]});Q4=makeQuery(id+"F10.imprint","IMPRINT",FACE,{"disambiguationData":[TD([[makeQuery(id+"F10.imprint","IMPRINT",EDGE,{"disambiguationData":[TD([[subQ2,-1.0]])],"derivedFrom":subQ1}),-1.0]])]});}
            var Q5;
            {var subQ1=sQuery(id+"F10.wireOp",EDGE,"E135.MirrorCS");Q5=makeQuery(id+"F10.imprint","IMPRINT",FACE,{"disambiguationData":[TD([[makeQuery(id+"F10.imprint","IMPRINT",EDGE,{"derivedFrom":subQ1}),-1.0]])]});}
            var Q6;
            {var subQ0=sQuery(id+"F10.wireOp",EDGE,"E134.MirrorCS");var subQ1=sQuery(id+"F10.wireOp",EDGE,"E133.MirrorCS");var subQ2=makeQuery(id+"F10.imprint","INTERSECT",VERTEX,{"derivedFrom":[subQ1,subQ0]});Q6=makeQuery(id+"F10.imprint","IMPRINT",FACE,{"disambiguationData":[TD([[makeQuery(id+"F10.imprint","IMPRINT",EDGE,{"disambiguationData":[TD([[subQ2,-1.0]])],"derivedFrom":subQ0}),1.0]])]});}
            var Q7;
            {var subQ0=sQuery(id+"F10.wireOp",EDGE,"E119.bottom");var subQ1=sQuery(id+"F10.wireOp",EDGE,"E119.right");var subQ2=makeQuery(id+"F10.imprint","INTERSECT",VERTEX,{"derivedFrom":[subQ1,subQ0]});Q7=makeQuery(id+"F10.imprint","IMPRINT",FACE,{"disambiguationData":[TD([[makeQuery(id+"F10.imprint","IMPRINT",EDGE,{"disambiguationData":[TD([[subQ2,-1.0]])],"derivedFrom":subQ1}),-1.0]])]});}
            var Q8;
            {var subQ0=sQuery(id+"F10.wireOp",EDGE,"E123.MirrorCS");var subQ1=sQuery(id+"F10.wireOp",EDGE,"E124.MirrorCS");var subQ2=makeQuery(id+"F10.imprint","INTERSECT",VERTEX,{"derivedFrom":[subQ1,subQ0]});Q8=makeQuery(id+"F10.imprint","IMPRINT",FACE,{"disambiguationData":[TD([[makeQuery(id+"F10.imprint","IMPRINT",EDGE,{"disambiguationData":[TD([[subQ2,1.0]])],"derivedFrom":subQ1}),-1.0]])]});}
            var Q9;
            {var subQ0=sQuery(id+"F10.wireOp",EDGE,"E136.MirrorCS");var subQ1=sQuery(id+"F10.wireOp",EDGE,"E134.MirrorCS");var subQ2=makeQuery(id+"F10.imprint","INTERSECT",VERTEX,{"derivedFrom":[subQ1,subQ0]});Q9=makeQuery(id+"F10.imprint","IMPRINT",FACE,{"disambiguationData":[TD([[makeQuery(id+"F10.imprint","IMPRINT",EDGE,{"disambiguationData":[TD([[subQ2,1.0]])],"derivedFrom":subQ1}),1.0]])]});}
            var Q10;
            {var subQ0=sQuery(id+"F10.wireOp",EDGE,"E130.MirrorCS");Q10=makeQuery(id+"F10.imprint","IMPRINT",FACE,{"disambiguationData":[TD([[makeQuery(id+"F10.imprint","IMPRINT",EDGE,{"derivedFrom":subQ0}),1.0]])]});}
            var Q11;
            {var subQ0=sQuery(id+"F10.wireOp",EDGE,"E131.MirrorCS");var subQ1=sQuery(id+"F10.wireOp",EDGE,"E129.MirrorCS");var subQ2=makeQuery(id+"F10.imprint","INTERSECT",VERTEX,{"derivedFrom":[subQ1,subQ0]});Q11=makeQuery(id+"F10.imprint","IMPRINT",FACE,{"disambiguationData":[TD([[makeQuery(id+"F10.imprint","IMPRINT",EDGE,{"disambiguationData":[TD([[subQ2,-1.0]])],"derivedFrom":subQ1}),-1.0]])]});}
            extrude(context, id + "F11", {"entities" : qUnion([Q0, Q1, Q2, Q3, Q4, Q5, Q6, Q7, Q8, Q9, Q10, Q11]), "operationType" : NewBodyOperationType.REMOVE, "endBound" : BoundingType.THROUGH_ALL, "oppositeDirection" : true, "depth" : 25 * mm});
        }
        {
            var Q0;
            Q0=makeQuery(id+"F2.opExtrude","SWEPT_BODY",BODY,{"disambiguationData":[OSD([sQuery(id+"F1.wireOp",EDGE,"E1"),sQuery(id+"F1.wireOp",EDGE,"E4.MirrorC"),sQuery(id+"F1.wireOp",EDGE,"E6.MirrorC"),sQuery(id+"F1.wireOp",EDGE,"E7.MirrorC"),sQuery(id+"F1.wireOp",EDGE,"E8"),sQuery(id+"F1.wireOp",EDGE,"E9.MirrorC"),sQuery(id+"F1.wireOp",EDGE,"E10.MirrorC"),sQuery(id+"F1.wireOp",EDGE,"E11.MirrorC"),sQuery(id+"F1.wireOp",EDGE,"E16"),sQuery(id+"F1.wireOp",EDGE,"E18"),sQuery(id+"F1.wireOp",EDGE,"E20.MirrorCS"),sQuery(id+"F1.wireOp",EDGE,"E22.MirrorCS")])]});
            var Q1;
            Q1=sQuery(id+"F3.wireOp",EDGE,"E26");
            transform(context, id + "F12", {"entities" : qUnion([Q0]), "transformType" : TransformType.ROTATION, "transformAxis" : qUnion([Q1]), "angle" : 90 * degree, "makeCopy" : true});
        }
        {
            var Q0;
            Q0=makeQuery(id+"F7.imprint","IMPRINT",FACE,{"disambiguationData":[TD([[makeQuery(id+"F7.imprint","IMPRINT",EDGE,{"derivedFrom":sQuery(id+"F7.wireOp",EDGE,"E52")}),1.0]])]});
            var sketch = newSketch(context, id + "F13", { "sketchPlane" : qUnion([Q0])});
            skLineSegment(sketch, "E138.0", {"start": v(-3.5, 14.58) * mm, "end": v(-10.5, 14.58) * mm});
            skLineSegment(sketch, "E138.1", {"start": v(-10.5, 12.08) * mm, "end": v(-10.5, 14.58) * mm});
            skLineSegment(sketch, "E138.2", {"start": v(-3.5, 12.08) * mm, "end": v(-10.5, 12.08) * mm});
            skLineSegment(sketch, "E138.3", {"start": v(-3.5, 12.08) * mm, "end": v(-3.5, 14.58) * mm});
            skLineSegment(sketch, "E138.4", {"start": v(-12.08, 3.5) * mm, "end": v(-12.08, 10.5) * mm});
            skLineSegment(sketch, "E138.5", {"start": v(-14.58, 10.5) * mm, "end": v(-12.08, 10.5) * mm});
            skLineSegment(sketch, "E138.6", {"start": v(-14.58, 3.5) * mm, "end": v(-14.58, 10.5) * mm});
            skLineSegment(sketch, "E138.7", {"start": v(-14.58, 3.5) * mm, "end": v(-12.08, 3.5) * mm});
            skLineSegment(sketch, "E139.MirrorCS", {"start": v(10.5, 12.08) * mm, "end": v(10.5, 14.58) * mm});
            skLineSegment(sketch, "E140.MirrorCS", {"start": v(3.5, 12.08) * mm, "end": v(10.5, 12.08) * mm});
            skLineSegment(sketch, "E141.MirrorCS", {"start": v(3.5, 12.08) * mm, "end": v(3.5, 14.58) * mm});
            skLineSegment(sketch, "E142.MirrorCS", {"start": v(14.58, 10.5) * mm, "end": v(12.08, 10.5) * mm});
            skLineSegment(sketch, "E143.MirrorCS", {"start": v(14.58, 3.5) * mm, "end": v(14.58, 10.5) * mm});
            skLineSegment(sketch, "E144.MirrorCS", {"start": v(3.5, 14.58) * mm, "end": v(10.5, 14.58) * mm});
            skLineSegment(sketch, "E145.MirrorCS", {"start": v(12.08, 3.5) * mm, "end": v(12.08, 10.5) * mm});
            skLineSegment(sketch, "E146.MirrorCS", {"start": v(14.58, 3.5) * mm, "end": v(12.08, 3.5) * mm});
            skLineSegment(sketch, "E147.MirrorCS", {"start": v(-14.58, -3.5) * mm, "end": v(-14.58, -10.5) * mm});
            skLineSegment(sketch, "E148.MirrorCS", {"start": v(14.58, -3.5) * mm, "end": v(14.58, -10.5) * mm});
            skLineSegment(sketch, "E149.MirrorCS", {"start": v(3.5, -12.08) * mm, "end": v(10.5, -12.08) * mm});
            skLineSegment(sketch, "E150.MirrorCS", {"start": v(3.5, -12.08) * mm, "end": v(3.5, -14.58) * mm});
            skLineSegment(sketch, "E151.MirrorCS", {"start": v(3.5, -14.58) * mm, "end": v(10.5, -14.58) * mm});
            skLineSegment(sketch, "E152.MirrorCS", {"start": v(10.5, -12.08) * mm, "end": v(10.5, -14.58) * mm});
            skLineSegment(sketch, "E153.MirrorCS", {"start": v(-14.58, -3.5) * mm, "end": v(-12.08, -3.5) * mm});
            skLineSegment(sketch, "E154.MirrorCS", {"start": v(-3.5, -12.08) * mm, "end": v(-3.5, -14.58) * mm});
            skLineSegment(sketch, "E155.MirrorCS", {"start": v(12.08, -3.5) * mm, "end": v(12.08, -10.5) * mm});
            skLineSegment(sketch, "E156.MirrorCS", {"start": v(-12.08, -3.5) * mm, "end": v(-12.08, -10.5) * mm});
            skLineSegment(sketch, "E157.MirrorCS", {"start": v(-3.5, -12.08) * mm, "end": v(-10.5, -12.08) * mm});
            skLineSegment(sketch, "E158.MirrorCS", {"start": v(14.58, -10.5) * mm, "end": v(12.08, -10.5) * mm});
            skLineSegment(sketch, "E159.MirrorCS", {"start": v(14.58, -3.5) * mm, "end": v(12.08, -3.5) * mm});
            skLineSegment(sketch, "E160.MirrorCS", {"start": v(-3.5, -14.58) * mm, "end": v(-10.5, -14.58) * mm});
            skLineSegment(sketch, "E161.MirrorCS", {"start": v(-14.58, -10.5) * mm, "end": v(-12.08, -10.5) * mm});
            skLineSegment(sketch, "E162.MirrorCS", {"start": v(-10.5, -12.08) * mm, "end": v(-10.5, -14.58) * mm});
            skPoint(sketch, "E163.center", {"position": v(0, 0) * mm});
            skSolve(sketch);
        }
        {
            var Q0;
            Q0 = qSketchRegion(id + "F13", true);
            var Q1;
            {var subQ0=sQuery(id+"F13.wireOp",EDGE,"E163.1.0");var subQ1=sQuery(id+"F13.wireOp",EDGE,"Tk42yfu5-2dGD-Ryp2-Gp2I-dcl0lD4qCTr1");var subQ2=makeQuery(id+"F13.imprint","INTERSECT",VERTEX,{"disambiguationData":[OD(0.0)],"derivedFrom":[subQ1,subQ0]});Q1=makeQuery(id+"F13.imprint","IMPRINT",FACE,{"disambiguationData":[TD([[makeQuery(id+"F13.imprint","IMPRINT",EDGE,{"disambiguationData":[TD([[subQ2,-1.0]])],"derivedFrom":subQ1}),1.0]])]});}
            extrude(context, id + "F14", {"entities" : qUnion([Q0, Q1]), "operationType" : NewBodyOperationType.REMOVE, "endBound" : BoundingType.THROUGH_ALL, "oppositeDirection" : true, "depth" : 25 * mm});
        }
    });
